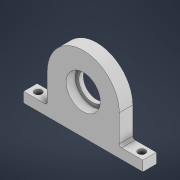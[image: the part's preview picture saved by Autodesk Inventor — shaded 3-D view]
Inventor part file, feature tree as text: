
AUTODESK INVENTOR PART (.ipt)
format: ipt  version: 2021 (Build 250183000, 183)  size: 307,200 bytes
history: native  units: mm
features: extrude x6, sketch x6, fillet x2, other x1
ambient origin geometry x8: Origin, YZ Plane, XZ Plane, XY Plane, X Axis, Y Axis, Z Axis, Center Point
bodies: Volumenkörper1 (feature_tree)
feature tree (15):
  other  "Halterung_Differential_Mitte"
  extrude  "Extrusion1"  Depth=32.0mm
  extrude  "Extrusion2"  Depth=10.5mm
  fillet  "Rundung1"  Radius=3.0mm
  fillet  "Rundung2"  Radius=6.0mm
  extrude  "Extrusion3"  Depth=1.0mm
  extrude  "Extrusion4"  Depth=4.0mm TaperAngle=0.0deg
  extrude  "Extrusion5"  Depth=5.0mm TaperAngle=0.0deg
  extrude  "Extrusion6"  Depth=3.0mm
  sketch  "Skizze1"  dims[d0=32.0mm d1=32.0mm]
  sketch  "Skizze2"  dims[d4=6.0mm d5=0.0mm d6=10.5mm d7=3.0mm d8=6.0mm d9=0.0mm]
  sketch  "Skizze3"  dims[d10=16.0mm d11=1.0mm]
  sketch  "Skizze4"  dims[d12=15.2mm d13=4.0mm d14=0.0mm]
  sketch  "Skizze5"  dims[d15=12.0mm d16=5.0mm d17=0.0mm]
  sketch  "Skizze6"  dims[d18=3.2mm d19=3.2mm d20=3.0mm d21=3.5mm d22=3.5mm d23=3.0mm d24=5.0mm d25=0.0mm d26=3.2mm d27=3.2mm d28=1.5mm d29=0.0mm]
